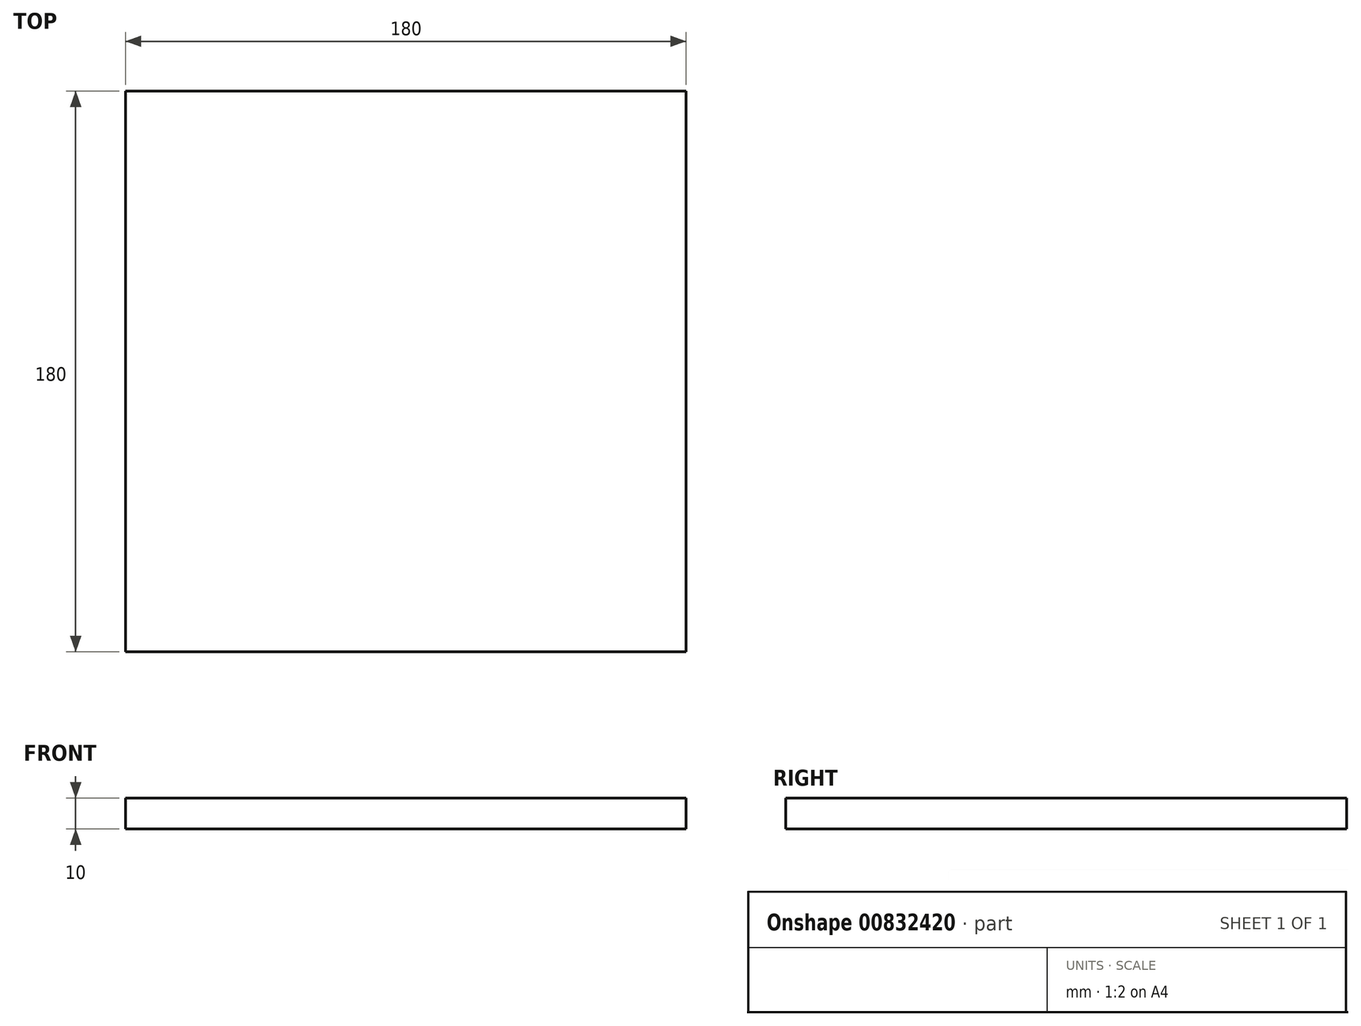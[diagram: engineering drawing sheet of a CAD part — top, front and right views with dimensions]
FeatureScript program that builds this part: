
annotation { "Feature Type Name" : "Feature", "Feature Type Description" : "" }
export const myFeature = defineFeature(function(context is Context, id is Id, definition is map)
    precondition{}
    {
        {
            var Q0;
            Q0=qCreatedBy(makeId("Top.planeOp"),FACE);
            var sketch = newSketch(context, id + "F0", { "sketchPlane" : qUnion([Q0])});
            skLineSegment(sketch, "E0.bottom", {"start": v(-90, 90) * mm, "end": v(90, 90) * mm});
            skLineSegment(sketch, "E0.top", {"start": v(-90, -90) * mm, "end": v(90, -90) * mm});
            skLineSegment(sketch, "E0.left", {"start": v(-90, 90) * mm, "end": v(-90, -90) * mm});
            skLineSegment(sketch, "E0.right", {"start": v(90, 90) * mm, "end": v(90, -90) * mm});
            skPoint(sketch, "E0.middle", {"position": v(0, 0) * mm});
            skSolve(sketch);
        }
        {
            var Q0;
            Q0=makeQuery(id+"F0.imprint","IMPRINT",FACE,{"disambiguationData":[TD([[makeQuery(id+"F0.imprint","IMPRINT",EDGE,{"derivedFrom":sQuery(id+"F0.wireOp",EDGE,"E0.bottom")}),-1.0]])]});
            extrude(context, id + "F1", {"entities" : qUnion([Q0]), "depth" : 10 * mm, "offsetDistance" : 25 * mm});
        }
    });
